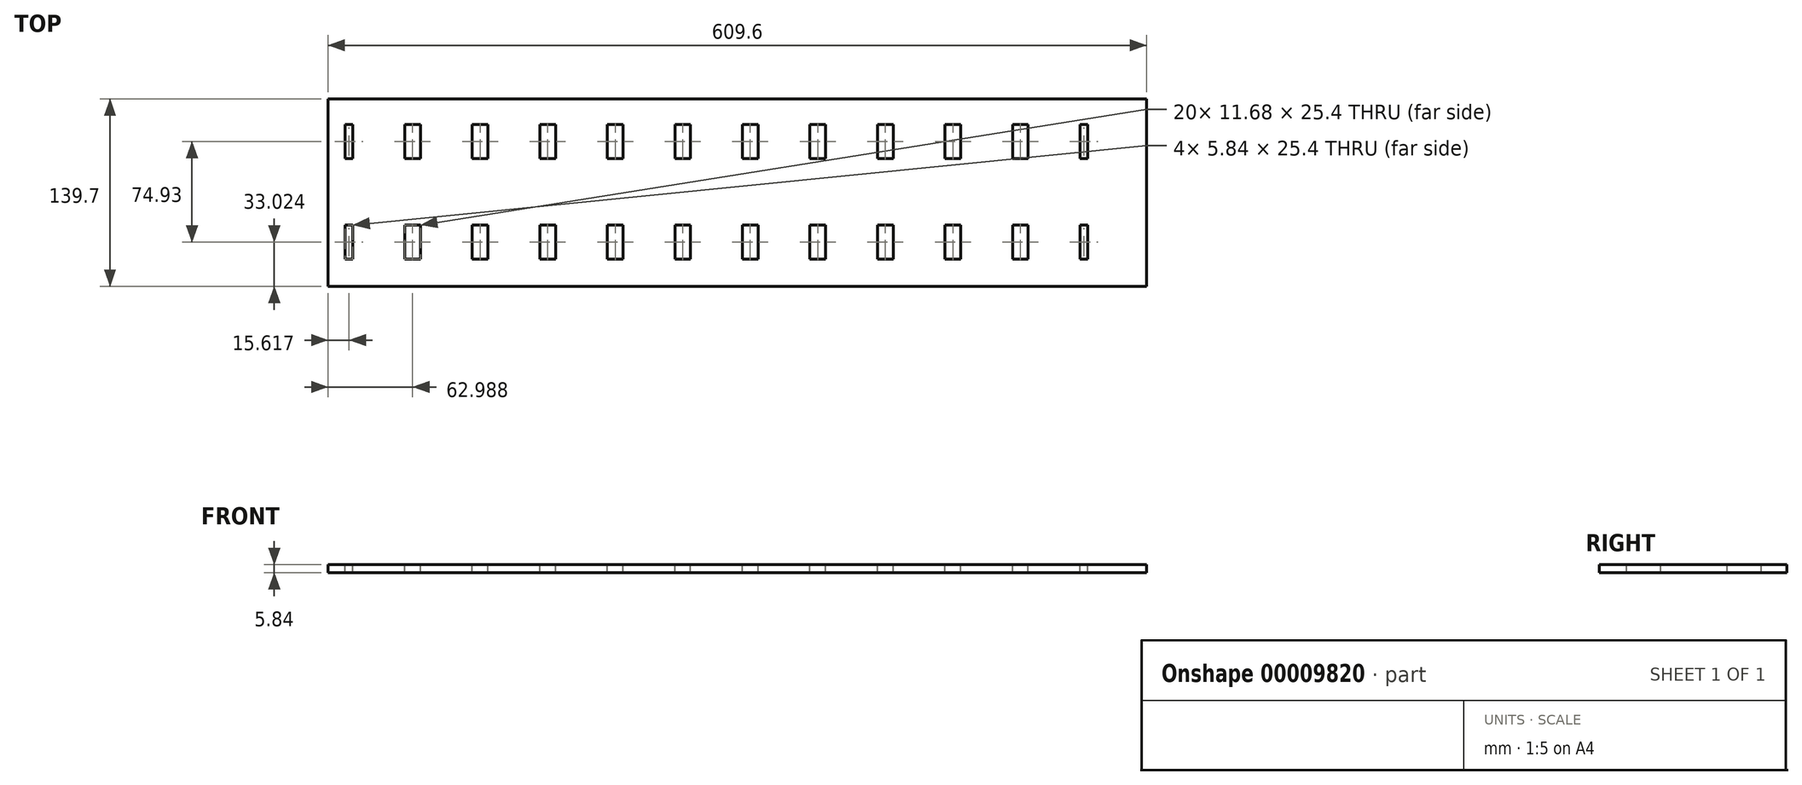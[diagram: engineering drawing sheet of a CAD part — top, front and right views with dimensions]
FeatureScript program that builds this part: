
annotation { "Feature Type Name" : "Feature", "Feature Type Description" : "" }
export const myFeature = defineFeature(function(context is Context, id is Id, definition is map)
    precondition{}
    {
        {
            var Q0;
            Q0=qCreatedBy(makeId("Top.planeOp"),FACE);
            var sketch = newSketch(context, id + "F0", { "sketchPlane" : qUnion([Q0])});
            skLineSegment(sketch, "E0.bottom", {"start": v(360.74, -82.02) * mm, "end": v(-248.86, -82.02) * mm});
            skLineSegment(sketch, "E0.top", {"start": v(360.74, 57.68) * mm, "end": v(-248.86, 57.68) * mm});
            skLineSegment(sketch, "E0.left", {"start": v(360.74, -82.02) * mm, "end": v(360.74, 57.68) * mm});
            skLineSegment(sketch, "E0.right", {"start": v(-248.86, -82.02) * mm, "end": v(-248.86, 57.68) * mm});
            skSolve(sketch);
        }
        {
            var Q0;
            Q0=makeQuery(id+"F0.imprint","IMPRINT",FACE,{"disambiguationData":[TD([[makeQuery(id+"F0.imprint","IMPRINT",EDGE,{"derivedFrom":sQuery(id+"F0.wireOp",EDGE,"E0.bottom")}),-1.0]])]});
            extrude(context, id + "F1", {"entities" : qUnion([Q0]), "oppositeDirection" : true, "depth" : 5.84 * mm});
        }
        {
            var Q0;
            Q0=makeQuery(id+"F1.opExtrude","CAP_FACE",FACE,{"disambiguationData":[OSD([sQuery(id+"F0.wireOp",EDGE,"E0.bottom"),sQuery(id+"F0.wireOp",EDGE,"E0.top"),sQuery(id+"F0.wireOp",EDGE,"E0.left"),sQuery(id+"F0.wireOp",EDGE,"E0.right")])],"isStart":true});
            var sketch = newSketch(context, id + "F2", { "sketchPlane" : qUnion([Q0])});
            skLineSegment(sketch, "E1.bottom", {"start": v(-236.16, 38.63) * mm, "end": v(-230.32, 38.63) * mm});
            skLineSegment(sketch, "E1.top", {"start": v(-236.16, 13.23) * mm, "end": v(-230.32, 13.23) * mm});
            skLineSegment(sketch, "E1.left", {"start": v(-236.16, 38.63) * mm, "end": v(-236.16, 13.23) * mm});
            skLineSegment(sketch, "E1.right", {"start": v(-230.32, 38.63) * mm, "end": v(-230.32, 13.23) * mm});
            skLineSegment(sketch, "E2.bottom", {"start": v(-236.16, -36.3) * mm, "end": v(-230.32, -36.3) * mm});
            skLineSegment(sketch, "E2.top", {"start": v(-236.16, -61.7) * mm, "end": v(-230.32, -61.7) * mm});
            skLineSegment(sketch, "E2.left", {"start": v(-236.16, -36.3) * mm, "end": v(-236.16, -61.7) * mm});
            skLineSegment(sketch, "E2.right", {"start": v(-230.32, -36.3) * mm, "end": v(-230.32, -61.7) * mm});
            skLineSegment(sketch, "E3.bottom", {"start": v(-236.16, -74.4) * mm, "end": v(-230.32, -74.4) * mm, "construction": true});
            skLineSegment(sketch, "E3.top", {"start": v(-236.16, 51.33) * mm, "end": v(-230.32, 51.33) * mm, "construction": true});
            skLineSegment(sketch, "E3.left", {"start": v(-236.16, -74.4) * mm, "end": v(-236.16, 51.33) * mm, "construction": true});
            skLineSegment(sketch, "E3.right", {"start": v(-230.32, -74.4) * mm, "end": v(-230.32, 51.33) * mm, "construction": true});
            skLineSegment(sketch, "E4.bottom", {"start": v(-191.71, 38.63) * mm, "end": v(-180.03, 38.63) * mm});
            skLineSegment(sketch, "E4.top", {"start": v(-191.71, 13.23) * mm, "end": v(-180.03, 13.23) * mm});
            skLineSegment(sketch, "E4.left", {"start": v(-191.71, 38.63) * mm, "end": v(-191.71, 13.23) * mm});
            skLineSegment(sketch, "E4.right", {"start": v(-180.03, 38.63) * mm, "end": v(-180.03, 13.23) * mm});
            skLineSegment(sketch, "E5.bottom", {"start": v(-191.71, -36.3) * mm, "end": v(-180.03, -36.3) * mm});
            skLineSegment(sketch, "E5.top", {"start": v(-191.71, -61.7) * mm, "end": v(-180.03, -61.7) * mm});
            skLineSegment(sketch, "E5.left", {"start": v(-191.71, -36.3) * mm, "end": v(-191.71, -61.7) * mm});
            skLineSegment(sketch, "E5.right", {"start": v(-180.03, -36.3) * mm, "end": v(-180.03, -61.7) * mm});
            skLineSegment(sketch, "E6.1.0.0", {"start": v(-141.42, 38.63) * mm, "end": v(-129.74, 38.63) * mm});
            skLineSegment(sketch, "E6.1.0.1", {"start": v(-141.42, 38.63) * mm, "end": v(-141.42, 13.23) * mm});
            skLineSegment(sketch, "E6.1.0.2", {"start": v(-129.74, 38.63) * mm, "end": v(-129.74, 13.23) * mm});
            skLineSegment(sketch, "E6.1.0.3", {"start": v(-141.42, 13.23) * mm, "end": v(-129.74, 13.23) * mm});
            skLineSegment(sketch, "E6.1.0.4", {"start": v(-141.42, -36.3) * mm, "end": v(-141.42, -61.7) * mm});
            skLineSegment(sketch, "E6.1.0.5", {"start": v(-141.42, -36.3) * mm, "end": v(-129.74, -36.3) * mm});
            skLineSegment(sketch, "E6.1.0.6", {"start": v(-129.74, -36.3) * mm, "end": v(-129.74, -61.7) * mm});
            skLineSegment(sketch, "E6.1.0.7", {"start": v(-141.42, -61.7) * mm, "end": v(-129.74, -61.7) * mm});
            skLineSegment(sketch, "E6.2.0.0", {"start": v(-91.13, 38.63) * mm, "end": v(-79.45, 38.63) * mm});
            skLineSegment(sketch, "E6.2.0.1", {"start": v(-91.13, 38.63) * mm, "end": v(-91.13, 13.23) * mm});
            skLineSegment(sketch, "E6.2.0.2", {"start": v(-79.45, 38.63) * mm, "end": v(-79.45, 13.23) * mm});
            skLineSegment(sketch, "E6.2.0.3", {"start": v(-91.13, 13.23) * mm, "end": v(-79.45, 13.23) * mm});
            skLineSegment(sketch, "E6.2.0.4", {"start": v(-91.13, -36.3) * mm, "end": v(-91.13, -61.7) * mm});
            skLineSegment(sketch, "E6.2.0.5", {"start": v(-91.13, -36.3) * mm, "end": v(-79.45, -36.3) * mm});
            skLineSegment(sketch, "E6.2.0.6", {"start": v(-79.45, -36.3) * mm, "end": v(-79.45, -61.7) * mm});
            skLineSegment(sketch, "E6.2.0.7", {"start": v(-91.13, -61.7) * mm, "end": v(-79.45, -61.7) * mm});
            skLineSegment(sketch, "E6.3.0.0", {"start": v(-40.84, 38.63) * mm, "end": v(-29.15, 38.63) * mm});
            skLineSegment(sketch, "E6.3.0.1", {"start": v(-40.84, 38.63) * mm, "end": v(-40.84, 13.23) * mm});
            skLineSegment(sketch, "E6.3.0.2", {"start": v(-29.15, 38.63) * mm, "end": v(-29.15, 13.23) * mm});
            skLineSegment(sketch, "E6.3.0.3", {"start": v(-40.84, 13.23) * mm, "end": v(-29.15, 13.23) * mm});
            skLineSegment(sketch, "E6.3.0.4", {"start": v(-40.84, -36.3) * mm, "end": v(-40.84, -61.7) * mm});
            skLineSegment(sketch, "E6.3.0.5", {"start": v(-40.84, -36.3) * mm, "end": v(-29.15, -36.3) * mm});
            skLineSegment(sketch, "E6.3.0.6", {"start": v(-29.15, -36.3) * mm, "end": v(-29.15, -61.7) * mm});
            skLineSegment(sketch, "E6.3.0.7", {"start": v(-40.84, -61.7) * mm, "end": v(-29.15, -61.7) * mm});
            skLineSegment(sketch, "E6.4.0.0", {"start": v(9.45, 38.63) * mm, "end": v(21.14, 38.63) * mm});
            skLineSegment(sketch, "E6.4.0.1", {"start": v(9.45, 38.63) * mm, "end": v(9.45, 13.23) * mm});
            skLineSegment(sketch, "E6.4.0.2", {"start": v(21.14, 38.63) * mm, "end": v(21.14, 13.23) * mm});
            skLineSegment(sketch, "E6.4.0.3", {"start": v(9.45, 13.23) * mm, "end": v(21.14, 13.23) * mm});
            skLineSegment(sketch, "E6.4.0.4", {"start": v(9.45, -36.3) * mm, "end": v(9.45, -61.7) * mm});
            skLineSegment(sketch, "E6.4.0.5", {"start": v(9.45, -36.3) * mm, "end": v(21.14, -36.3) * mm});
            skLineSegment(sketch, "E6.4.0.6", {"start": v(21.14, -36.3) * mm, "end": v(21.14, -61.7) * mm});
            skLineSegment(sketch, "E6.4.0.7", {"start": v(9.45, -61.7) * mm, "end": v(21.14, -61.7) * mm});
            skLineSegment(sketch, "E6.5.0.0", {"start": v(59.75, 38.63) * mm, "end": v(71.43, 38.63) * mm});
            skLineSegment(sketch, "E6.5.0.1", {"start": v(59.75, 38.63) * mm, "end": v(59.75, 13.23) * mm});
            skLineSegment(sketch, "E6.5.0.2", {"start": v(71.43, 38.63) * mm, "end": v(71.43, 13.23) * mm});
            skLineSegment(sketch, "E6.5.0.3", {"start": v(59.75, 13.23) * mm, "end": v(71.43, 13.23) * mm});
            skLineSegment(sketch, "E6.5.0.4", {"start": v(59.75, -36.3) * mm, "end": v(59.75, -61.7) * mm});
            skLineSegment(sketch, "E6.5.0.5", {"start": v(59.75, -36.3) * mm, "end": v(71.43, -36.3) * mm});
            skLineSegment(sketch, "E6.5.0.6", {"start": v(71.43, -36.3) * mm, "end": v(71.43, -61.7) * mm});
            skLineSegment(sketch, "E6.5.0.7", {"start": v(59.75, -61.7) * mm, "end": v(71.43, -61.7) * mm});
            skLineSegment(sketch, "E6.6.0.0", {"start": v(110.04, 38.63) * mm, "end": v(121.72, 38.63) * mm});
            skLineSegment(sketch, "E6.6.0.1", {"start": v(110.04, 38.63) * mm, "end": v(110.04, 13.23) * mm});
            skLineSegment(sketch, "E6.6.0.2", {"start": v(121.72, 38.63) * mm, "end": v(121.72, 13.23) * mm});
            skLineSegment(sketch, "E6.6.0.3", {"start": v(110.04, 13.23) * mm, "end": v(121.72, 13.23) * mm});
            skLineSegment(sketch, "E6.6.0.4", {"start": v(110.04, -36.3) * mm, "end": v(110.04, -61.7) * mm});
            skLineSegment(sketch, "E6.6.0.5", {"start": v(110.04, -36.3) * mm, "end": v(121.72, -36.3) * mm});
            skLineSegment(sketch, "E6.6.0.6", {"start": v(121.72, -36.3) * mm, "end": v(121.72, -61.7) * mm});
            skLineSegment(sketch, "E6.6.0.7", {"start": v(110.04, -61.7) * mm, "end": v(121.72, -61.7) * mm});
            skLineSegment(sketch, "E6.7.0.0", {"start": v(160.33, 38.63) * mm, "end": v(172.01, 38.63) * mm});
            skLineSegment(sketch, "E6.7.0.1", {"start": v(160.33, 38.63) * mm, "end": v(160.33, 13.23) * mm});
            skLineSegment(sketch, "E6.7.0.2", {"start": v(172.01, 38.63) * mm, "end": v(172.01, 13.23) * mm});
            skLineSegment(sketch, "E6.7.0.3", {"start": v(160.33, 13.23) * mm, "end": v(172.01, 13.23) * mm});
            skLineSegment(sketch, "E6.7.0.4", {"start": v(160.33, -36.3) * mm, "end": v(160.33, -61.7) * mm});
            skLineSegment(sketch, "E6.7.0.5", {"start": v(160.33, -36.3) * mm, "end": v(172.01, -36.3) * mm});
            skLineSegment(sketch, "E6.7.0.6", {"start": v(172.01, -36.3) * mm, "end": v(172.01, -61.7) * mm});
            skLineSegment(sketch, "E6.7.0.7", {"start": v(160.33, -61.7) * mm, "end": v(172.01, -61.7) * mm});
            skLineSegment(sketch, "E6.8.0.0", {"start": v(210.62, 38.63) * mm, "end": v(222.3, 38.63) * mm});
            skLineSegment(sketch, "E6.8.0.1", {"start": v(210.62, 38.63) * mm, "end": v(210.62, 13.23) * mm});
            skLineSegment(sketch, "E6.8.0.2", {"start": v(222.3, 38.63) * mm, "end": v(222.3, 13.23) * mm});
            skLineSegment(sketch, "E6.8.0.3", {"start": v(210.62, 13.23) * mm, "end": v(222.3, 13.23) * mm});
            skLineSegment(sketch, "E6.8.0.4", {"start": v(210.62, -36.3) * mm, "end": v(210.62, -61.7) * mm});
            skLineSegment(sketch, "E6.8.0.5", {"start": v(210.62, -36.3) * mm, "end": v(222.3, -36.3) * mm});
            skLineSegment(sketch, "E6.8.0.6", {"start": v(222.3, -36.3) * mm, "end": v(222.3, -61.7) * mm});
            skLineSegment(sketch, "E6.8.0.7", {"start": v(210.62, -61.7) * mm, "end": v(222.3, -61.7) * mm});
            skLineSegment(sketch, "E6.9.0.0", {"start": v(260.91, 38.63) * mm, "end": v(272.6, 38.63) * mm});
            skLineSegment(sketch, "E6.9.0.1", {"start": v(260.91, 38.63) * mm, "end": v(260.91, 13.23) * mm});
            skLineSegment(sketch, "E6.9.0.2", {"start": v(272.6, 38.63) * mm, "end": v(272.6, 13.23) * mm});
            skLineSegment(sketch, "E6.9.0.3", {"start": v(260.91, 13.23) * mm, "end": v(272.6, 13.23) * mm});
            skLineSegment(sketch, "E6.9.0.4", {"start": v(260.91, -36.3) * mm, "end": v(260.91, -61.7) * mm});
            skLineSegment(sketch, "E6.9.0.5", {"start": v(260.91, -36.3) * mm, "end": v(272.6, -36.3) * mm});
            skLineSegment(sketch, "E6.9.0.6", {"start": v(272.6, -36.3) * mm, "end": v(272.6, -61.7) * mm});
            skLineSegment(sketch, "E6.9.0.7", {"start": v(260.91, -61.7) * mm, "end": v(272.6, -61.7) * mm});
            skLineSegment(sketch, "E6.direction1", {"start": v(-191.71, 38.63) * mm, "end": v(-141.42, 38.63) * mm, "construction": true});
            skLineSegment(sketch, "E7.bottom", {"start": v(311.2, 38.63) * mm, "end": v(317.05, 38.63) * mm});
            skLineSegment(sketch, "E7.top", {"start": v(311.2, 13.23) * mm, "end": v(317.05, 13.23) * mm});
            skLineSegment(sketch, "E7.left", {"start": v(311.2, 38.63) * mm, "end": v(311.2, 13.23) * mm});
            skLineSegment(sketch, "E7.right", {"start": v(317.05, 38.63) * mm, "end": v(317.05, 13.23) * mm});
            skLineSegment(sketch, "E8.bottom", {"start": v(311.2, -36.3) * mm, "end": v(317.05, -36.3) * mm});
            skLineSegment(sketch, "E8.top", {"start": v(311.2, -61.7) * mm, "end": v(317.05, -61.7) * mm});
            skLineSegment(sketch, "E8.left", {"start": v(311.2, -36.3) * mm, "end": v(311.2, -61.7) * mm});
            skLineSegment(sketch, "E8.right", {"start": v(317.05, -36.3) * mm, "end": v(317.05, -61.7) * mm});
            skSolve(sketch);
        }
        {
            var Q0;
            Q0=makeQuery(id+"F2.imprint","IMPRINT",FACE,{"disambiguationData":[TD([[makeQuery(id+"F2.imprint","IMPRINT",EDGE,{"derivedFrom":sQuery(id+"F2.wireOp",EDGE,"E1.bottom")}),-1.0]])]});
            var Q1;
            Q1=makeQuery(id+"F2.imprint","IMPRINT",FACE,{"disambiguationData":[TD([[makeQuery(id+"F2.imprint","IMPRINT",EDGE,{"derivedFrom":sQuery(id+"F2.wireOp",EDGE,"E2.bottom")}),-1.0]])]});
            var Q2;
            Q2=makeQuery(id+"F2.imprint","IMPRINT",FACE,{"disambiguationData":[TD([[makeQuery(id+"F2.imprint","IMPRINT",EDGE,{"derivedFrom":sQuery(id+"F2.wireOp",EDGE,"E5.bottom")}),-1.0]])]});
            var Q3;
            Q3=makeQuery(id+"F2.imprint","IMPRINT",FACE,{"disambiguationData":[TD([[makeQuery(id+"F2.imprint","IMPRINT",EDGE,{"derivedFrom":sQuery(id+"F2.wireOp",EDGE,"E4.bottom")}),-1.0]])]});
            var Q4;
            Q4=makeQuery(id+"F2.imprint","IMPRINT",FACE,{"disambiguationData":[TD([[makeQuery(id+"F2.imprint","IMPRINT",EDGE,{"derivedFrom":sQuery(id+"F2.wireOp",EDGE,"E6.1.0.0")}),-1.0]])]});
            var Q5;
            Q5=makeQuery(id+"F2.imprint","IMPRINT",FACE,{"disambiguationData":[TD([[makeQuery(id+"F2.imprint","IMPRINT",EDGE,{"derivedFrom":sQuery(id+"F2.wireOp",EDGE,"E6.1.0.4")}),1.0]])]});
            var Q6;
            Q6=makeQuery(id+"F2.imprint","IMPRINT",FACE,{"disambiguationData":[TD([[makeQuery(id+"F2.imprint","IMPRINT",EDGE,{"derivedFrom":sQuery(id+"F2.wireOp",EDGE,"E6.2.0.4")}),1.0]])]});
            var Q7;
            Q7=makeQuery(id+"F2.imprint","IMPRINT",FACE,{"disambiguationData":[TD([[makeQuery(id+"F2.imprint","IMPRINT",EDGE,{"derivedFrom":sQuery(id+"F2.wireOp",EDGE,"E6.2.0.0")}),-1.0]])]});
            var Q8;
            Q8=makeQuery(id+"F2.imprint","IMPRINT",FACE,{"disambiguationData":[TD([[makeQuery(id+"F2.imprint","IMPRINT",EDGE,{"derivedFrom":sQuery(id+"F2.wireOp",EDGE,"E6.3.0.0")}),-1.0]])]});
            var Q9;
            Q9=makeQuery(id+"F2.imprint","IMPRINT",FACE,{"disambiguationData":[TD([[makeQuery(id+"F2.imprint","IMPRINT",EDGE,{"derivedFrom":sQuery(id+"F2.wireOp",EDGE,"E6.3.0.4")}),1.0]])]});
            var Q10;
            Q10=makeQuery(id+"F2.imprint","IMPRINT",FACE,{"disambiguationData":[TD([[makeQuery(id+"F2.imprint","IMPRINT",EDGE,{"derivedFrom":sQuery(id+"F2.wireOp",EDGE,"E6.4.0.4")}),1.0]])]});
            var Q11;
            Q11=makeQuery(id+"F2.imprint","IMPRINT",FACE,{"disambiguationData":[TD([[makeQuery(id+"F2.imprint","IMPRINT",EDGE,{"derivedFrom":sQuery(id+"F2.wireOp",EDGE,"E6.4.0.0")}),-1.0]])]});
            var Q12;
            Q12=makeQuery(id+"F2.imprint","IMPRINT",FACE,{"disambiguationData":[TD([[makeQuery(id+"F2.imprint","IMPRINT",EDGE,{"derivedFrom":sQuery(id+"F2.wireOp",EDGE,"E6.5.0.0")}),-1.0]])]});
            var Q13;
            Q13=makeQuery(id+"F2.imprint","IMPRINT",FACE,{"disambiguationData":[TD([[makeQuery(id+"F2.imprint","IMPRINT",EDGE,{"derivedFrom":sQuery(id+"F2.wireOp",EDGE,"E6.5.0.4")}),1.0]])]});
            var Q14;
            Q14=makeQuery(id+"F2.imprint","IMPRINT",FACE,{"disambiguationData":[TD([[makeQuery(id+"F2.imprint","IMPRINT",EDGE,{"derivedFrom":sQuery(id+"F2.wireOp",EDGE,"E6.6.0.4")}),1.0]])]});
            var Q15;
            Q15=makeQuery(id+"F2.imprint","IMPRINT",FACE,{"disambiguationData":[TD([[makeQuery(id+"F2.imprint","IMPRINT",EDGE,{"derivedFrom":sQuery(id+"F2.wireOp",EDGE,"E6.6.0.0")}),-1.0]])]});
            var Q16;
            Q16=makeQuery(id+"F2.imprint","IMPRINT",FACE,{"disambiguationData":[TD([[makeQuery(id+"F2.imprint","IMPRINT",EDGE,{"derivedFrom":sQuery(id+"F2.wireOp",EDGE,"E6.7.0.0")}),-1.0]])]});
            var Q17;
            Q17=makeQuery(id+"F2.imprint","IMPRINT",FACE,{"disambiguationData":[TD([[makeQuery(id+"F2.imprint","IMPRINT",EDGE,{"derivedFrom":sQuery(id+"F2.wireOp",EDGE,"E6.7.0.4")}),1.0]])]});
            var Q18;
            Q18=makeQuery(id+"F2.imprint","IMPRINT",FACE,{"disambiguationData":[TD([[makeQuery(id+"F2.imprint","IMPRINT",EDGE,{"derivedFrom":sQuery(id+"F2.wireOp",EDGE,"E6.8.0.4")}),1.0]])]});
            var Q19;
            Q19=makeQuery(id+"F2.imprint","IMPRINT",FACE,{"disambiguationData":[TD([[makeQuery(id+"F2.imprint","IMPRINT",EDGE,{"derivedFrom":sQuery(id+"F2.wireOp",EDGE,"E6.8.0.0")}),-1.0]])]});
            var Q20;
            Q20=makeQuery(id+"F2.imprint","IMPRINT",FACE,{"disambiguationData":[TD([[makeQuery(id+"F2.imprint","IMPRINT",EDGE,{"derivedFrom":sQuery(id+"F2.wireOp",EDGE,"E6.9.0.4")}),1.0]])]});
            var Q21;
            Q21=makeQuery(id+"F2.imprint","IMPRINT",FACE,{"disambiguationData":[TD([[makeQuery(id+"F2.imprint","IMPRINT",EDGE,{"derivedFrom":sQuery(id+"F2.wireOp",EDGE,"E6.9.0.0")}),-1.0]])]});
            var Q22;
            Q22=makeQuery(id+"F2.imprint","IMPRINT",FACE,{"disambiguationData":[TD([[makeQuery(id+"F2.imprint","IMPRINT",EDGE,{"derivedFrom":sQuery(id+"F2.wireOp",EDGE,"E6.10.0.0")}),-1.0]])]});
            var Q23;
            Q23=makeQuery(id+"F2.imprint","IMPRINT",FACE,{"disambiguationData":[TD([[makeQuery(id+"F2.imprint","IMPRINT",EDGE,{"derivedFrom":sQuery(id+"F2.wireOp",EDGE,"E6.10.0.4")}),1.0]])]});
            var Q24;
            Q24=makeQuery(id+"F2.imprint","IMPRINT",FACE,{"disambiguationData":[TD([[makeQuery(id+"F2.imprint","IMPRINT",EDGE,{"derivedFrom":sQuery(id+"F2.wireOp",EDGE,"E6.11.0.4")}),1.0]])]});
            var Q25;
            Q25=makeQuery(id+"F2.imprint","IMPRINT",FACE,{"disambiguationData":[TD([[makeQuery(id+"F2.imprint","IMPRINT",EDGE,{"derivedFrom":sQuery(id+"F2.wireOp",EDGE,"E6.11.0.0")}),-1.0]])]});
            var Q26;
            Q26=makeQuery(id+"F2.imprint","IMPRINT",FACE,{"disambiguationData":[TD([[makeQuery(id+"F2.imprint","IMPRINT",EDGE,{"derivedFrom":sQuery(id+"F2.wireOp",EDGE,"E6.12.0.0")}),-1.0]])]});
            var Q27;
            Q27=makeQuery(id+"F2.imprint","IMPRINT",FACE,{"disambiguationData":[TD([[makeQuery(id+"F2.imprint","IMPRINT",EDGE,{"derivedFrom":sQuery(id+"F2.wireOp",EDGE,"E6.12.0.4")}),1.0]])]});
            var Q28;
            Q28=makeQuery(id+"F2.imprint","IMPRINT",FACE,{"disambiguationData":[TD([[makeQuery(id+"F2.imprint","IMPRINT",EDGE,{"derivedFrom":sQuery(id+"F2.wireOp",EDGE,"E6.13.0.4")}),1.0]])]});
            var Q29;
            Q29=makeQuery(id+"F2.imprint","IMPRINT",FACE,{"disambiguationData":[TD([[makeQuery(id+"F2.imprint","IMPRINT",EDGE,{"derivedFrom":sQuery(id+"F2.wireOp",EDGE,"E6.13.0.0")}),-1.0]])]});
            var Q30;
            Q30=makeQuery(id+"F2.imprint","IMPRINT",FACE,{"disambiguationData":[TD([[makeQuery(id+"F2.imprint","IMPRINT",EDGE,{"derivedFrom":sQuery(id+"F2.wireOp",EDGE,"E6.14.0.0")}),-1.0]])]});
            var Q31;
            Q31=makeQuery(id+"F2.imprint","IMPRINT",FACE,{"disambiguationData":[TD([[makeQuery(id+"F2.imprint","IMPRINT",EDGE,{"derivedFrom":sQuery(id+"F2.wireOp",EDGE,"E6.14.0.4")}),1.0]])]});
            var Q32;
            Q32=makeQuery(id+"F2.imprint","IMPRINT",FACE,{"disambiguationData":[TD([[makeQuery(id+"F2.imprint","IMPRINT",EDGE,{"derivedFrom":sQuery(id+"F2.wireOp",EDGE,"E6.15.0.4")}),1.0]])]});
            var Q33;
            Q33=makeQuery(id+"F2.imprint","IMPRINT",FACE,{"disambiguationData":[TD([[makeQuery(id+"F2.imprint","IMPRINT",EDGE,{"derivedFrom":sQuery(id+"F2.wireOp",EDGE,"E6.15.0.0")}),-1.0]])]});
            var Q34;
            Q34=makeQuery(id+"F2.imprint","IMPRINT",FACE,{"disambiguationData":[TD([[makeQuery(id+"F2.imprint","IMPRINT",EDGE,{"derivedFrom":sQuery(id+"F2.wireOp",EDGE,"E6.16.0.0")}),-1.0]])]});
            var Q35;
            Q35=makeQuery(id+"F2.imprint","IMPRINT",FACE,{"disambiguationData":[TD([[makeQuery(id+"F2.imprint","IMPRINT",EDGE,{"derivedFrom":sQuery(id+"F2.wireOp",EDGE,"E6.16.0.4")}),1.0]])]});
            var Q36;
            Q36=makeQuery(id+"F2.imprint","IMPRINT",FACE,{"disambiguationData":[TD([[makeQuery(id+"F2.imprint","IMPRINT",EDGE,{"derivedFrom":sQuery(id+"F2.wireOp",EDGE,"E7.bottom")}),-1.0]])]});
            var Q37;
            Q37=makeQuery(id+"F2.imprint","IMPRINT",FACE,{"disambiguationData":[TD([[makeQuery(id+"F2.imprint","IMPRINT",EDGE,{"derivedFrom":sQuery(id+"F2.wireOp",EDGE,"E8.bottom")}),-1.0]])]});
            extrude(context, id + "F3", {"entities" : qUnion([Q0, Q1, Q2, Q3, Q4, Q5, Q6, Q7, Q8, Q9, Q10, Q11, Q12, Q13, Q14, Q15, Q16, Q17, Q18, Q19, Q20, Q21, Q22, Q23, Q24, Q25, Q26, Q27, Q28, Q29, Q30, Q31, Q32, Q33, Q34, Q35, Q36, Q37]), "operationType" : NewBodyOperationType.REMOVE, "oppositeDirection" : true, "depth" : 25.4 * mm});
        }
    });
